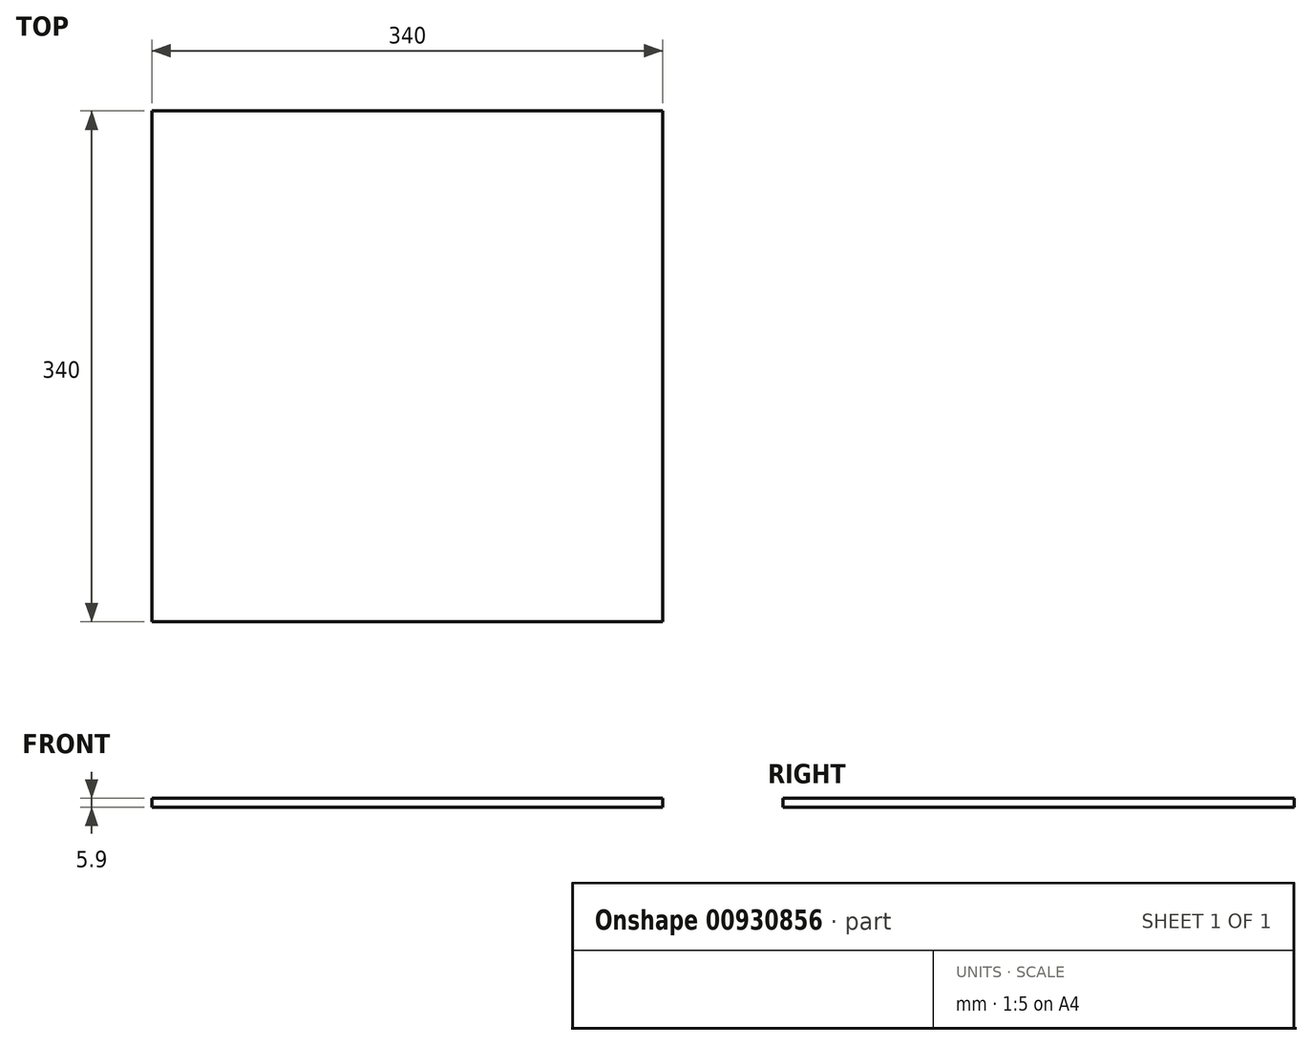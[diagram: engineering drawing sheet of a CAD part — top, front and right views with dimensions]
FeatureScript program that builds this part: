
annotation { "Feature Type Name" : "Feature", "Feature Type Description" : "" }
export const myFeature = defineFeature(function(context is Context, id is Id, definition is map)
    precondition{}
    {
        {
            var Q0;
            Q0=qCreatedBy(makeId("Top.planeOp"),FACE);
            var sketch = newSketch(context, id + "F0", { "sketchPlane" : qUnion([Q0])});
            skLineSegment(sketch, "E0.bottom", {"start": v(170, -170) * mm, "end": v(-170, -170) * mm});
            skLineSegment(sketch, "E0.top", {"start": v(170, 170) * mm, "end": v(-170, 170) * mm});
            skLineSegment(sketch, "E0.left", {"start": v(170, -170) * mm, "end": v(170, 170) * mm});
            skLineSegment(sketch, "E0.right", {"start": v(-170, -170) * mm, "end": v(-170, 170) * mm});
            skPoint(sketch, "E0.middle", {"position": v(0, 0) * mm});
            skSolve(sketch);
        }
        {
            var Q0;
            Q0=makeQuery(id+"F0.imprint","IMPRINT",FACE,{"disambiguationData":[TD([[makeQuery(id+"F0.imprint","IMPRINT",EDGE,{"derivedFrom":sQuery(id+"F0.wireOp",EDGE,"E0.bottom")}),-1.0]])]});
            extrude(context, id + "F1", {"entities" : qUnion([Q0]), "depth" : 5.9 * mm, "offsetDistance" : 25 * mm});
        }
    });
